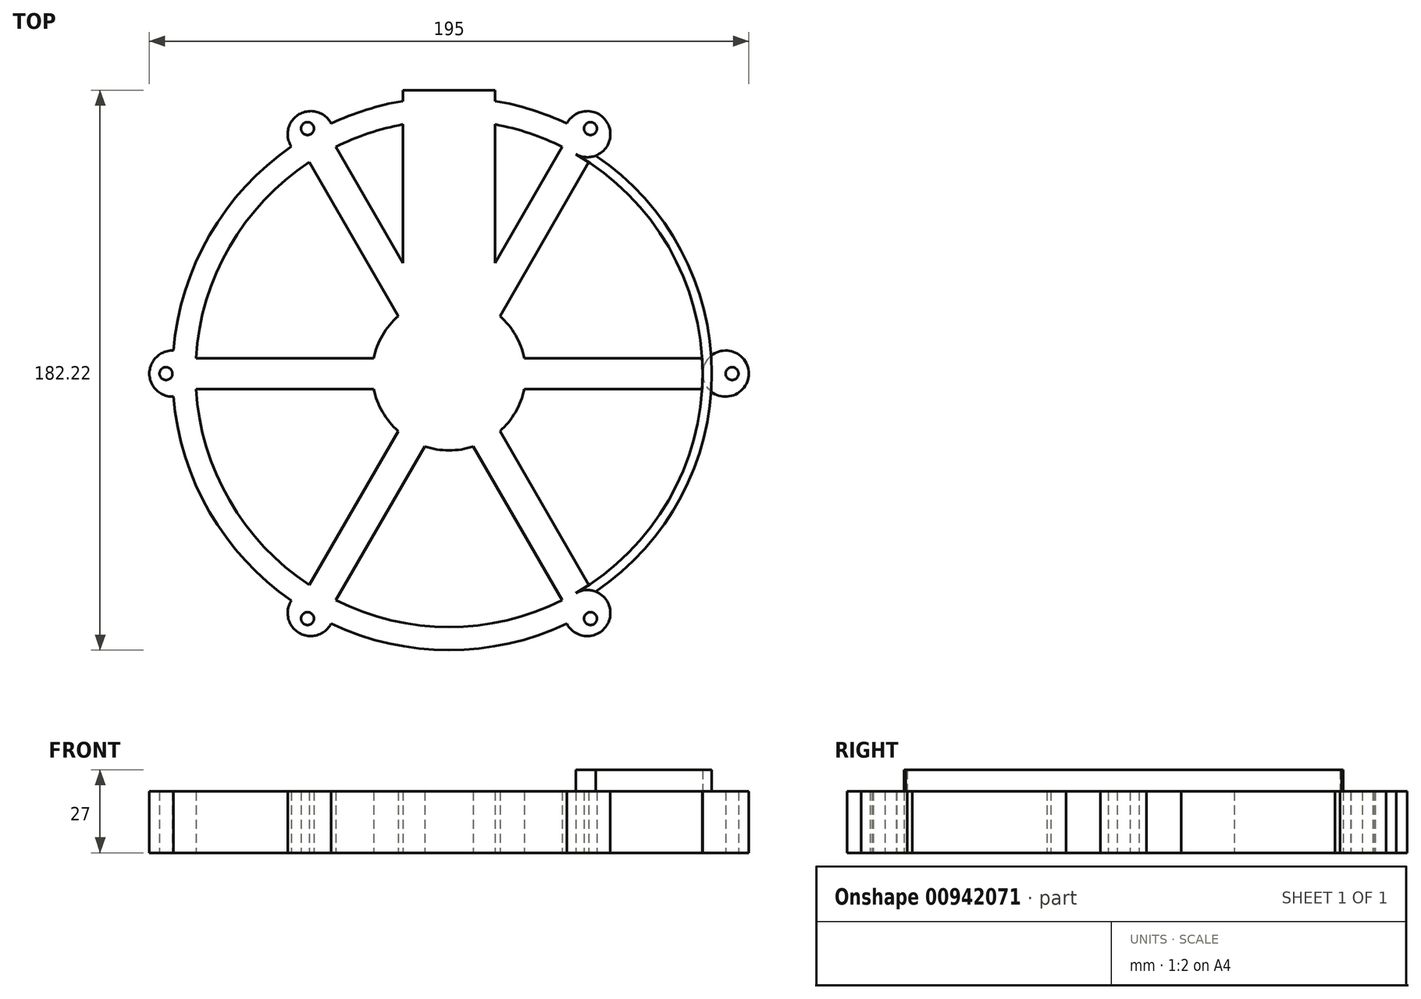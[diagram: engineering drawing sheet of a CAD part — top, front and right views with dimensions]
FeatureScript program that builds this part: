
annotation { "Feature Type Name" : "Feature", "Feature Type Description" : "" }
export const myFeature = defineFeature(function(context is Context, id is Id, definition is map)
    precondition{}
    {
        {
            var Q0;
            Q0=qCreatedBy(makeId("Top.planeOp"),FACE);
            var sketch = newSketch(context, id + "F0", { "sketchPlane" : qUnion([Q0])});
            skCircle(sketch, "E0", {"center": v(0, 0) * mm, "radius": 90 * mm});
            skCircle(sketch, "E1", {"center": v(0, 0) * mm, "radius": 82.5 * mm});
            skCircle(sketch, "E2", {"center": v(0, 0) * mm, "radius": 25 * mm});
            skLineSegment(sketch, "E3", {"start": v(45.5, 68.82) * mm, "end": v(16.58, 18.71) * mm});
            skLineSegment(sketch, "E4.MirrorCS", {"start": v(36.84, 73.82) * mm, "end": v(7.92, 23.71) * mm});
            skLineSegment(sketch, "E5.1.0", {"start": v(-36.84, 73.82) * mm, "end": v(-7.92, 23.71) * mm});
            skLineSegment(sketch, "E5.1.1", {"start": v(-45.5, 68.82) * mm, "end": v(-16.58, 18.71) * mm});
            skLineSegment(sketch, "E5.2.0", {"start": v(-82.35, 5) * mm, "end": v(-24.5, 5) * mm});
            skLineSegment(sketch, "E5.2.1", {"start": v(-82.35, -5) * mm, "end": v(-24.5, -5) * mm});
            skLineSegment(sketch, "E5.3.0", {"start": v(-45.5, -68.82) * mm, "end": v(-16.58, -18.71) * mm});
            skLineSegment(sketch, "E5.3.1", {"start": v(-36.84, -73.82) * mm, "end": v(-7.92, -23.71) * mm});
            skLineSegment(sketch, "E5.4.0", {"start": v(36.84, -73.82) * mm, "end": v(7.92, -23.71) * mm});
            skLineSegment(sketch, "E5.4.1", {"start": v(45.5, -68.82) * mm, "end": v(16.58, -18.71) * mm});
            skLineSegment(sketch, "E5.5.0", {"start": v(82.35, -5) * mm, "end": v(24.5, -5) * mm});
            skLineSegment(sketch, "E5.5.1", {"start": v(82.35, 5) * mm, "end": v(24.5, 5) * mm});
            skCircle(sketch, "E6", {"center": v(45, 77.94) * mm, "radius": 7.5 * mm});
            skCircle(sketch, "E7", {"center": v(46.05, 79.76) * mm, "radius": 2.1 * mm});
            skCircle(sketch, "E8.1.0", {"center": v(-45, 77.94) * mm, "radius": 7.5 * mm});
            skCircle(sketch, "E8.1.1", {"center": v(-46.05, 79.76) * mm, "radius": 2.1 * mm});
            skCircle(sketch, "E8.2.0", {"center": v(-90, 0) * mm, "radius": 7.5 * mm});
            skCircle(sketch, "E8.2.1", {"center": v(-92.1, 0) * mm, "radius": 2.1 * mm});
            skCircle(sketch, "E8.3.0", {"center": v(-45, -77.94) * mm, "radius": 7.5 * mm});
            skCircle(sketch, "E8.3.1", {"center": v(-46.05, -79.76) * mm, "radius": 2.1 * mm});
            skCircle(sketch, "E8.4.0", {"center": v(45, -77.94) * mm, "radius": 7.5 * mm});
            skCircle(sketch, "E8.4.1", {"center": v(46.05, -79.76) * mm, "radius": 2.1 * mm});
            skCircle(sketch, "E8.5.0", {"center": v(90, 0) * mm, "radius": 7.5 * mm});
            skCircle(sketch, "E8.5.1", {"center": v(92.1, 0) * mm, "radius": 2.1 * mm});
            skLineSegment(sketch, "E9", {"start": v(15, 35.98) * mm, "end": v(15, 92.22) * mm});
            skLineSegment(sketch, "E10.MirrorCS", {"start": v(-15, 35.98) * mm, "end": v(-15, 92.22) * mm});
            skLineSegment(sketch, "E11", {"start": v(-15, 92.22) * mm, "end": v(15, 92.22) * mm});
            skSolve(sketch);
        }
        {
            var Q0;
            {var subQ4=sQuery(id+"F0.wireOp",EDGE,"E0");var subQ7=sQuery(id+"F0.wireOp",EDGE,"E8.1.0");var subQ9=makeQuery(id+"F0.imprint","INTERSECT",VERTEX,{"disambiguationData":[OD(1.0)],"derivedFrom":[subQ4,subQ7]});Q0=makeQuery(id+"F0.imprint","IMPRINT",FACE,{"disambiguationData":[TD([[makeQuery(id+"F0.imprint","IMPRINT",EDGE,{"disambiguationData":[TD([[subQ9,-1.0]])],"derivedFrom":subQ4}),1.0]])]});}
            var Q1;
            {var subQ0=sQuery(id+"F0.wireOp",EDGE,"E8.1.0");var subQ1=sQuery(id+"F0.wireOp",EDGE,"E0");var subQ2=makeQuery(id+"F0.imprint","INTERSECT",VERTEX,{"disambiguationData":[OD(0.0)],"derivedFrom":[subQ1,subQ0]});Q1=makeQuery(id+"F0.imprint","IMPRINT",FACE,{"disambiguationData":[TD([[makeQuery(id+"F0.imprint","IMPRINT",EDGE,{"disambiguationData":[TD([[subQ2,-1.0]])],"derivedFrom":subQ1}),1.0]])]});}
            var Q2;
            {var subQ3=sQuery(id+"F0.wireOp",EDGE,"E8.1.1");Q2=makeQuery(id+"F0.imprint","IMPRINT",FACE,{"disambiguationData":[TD([[makeQuery(id+"F0.imprint","IMPRINT",EDGE,{"derivedFrom":subQ3}),-1.0]])]});}
            var Q3;
            {var subQ1=sQuery(id+"F0.wireOp",EDGE,"E0");var subQ6=sQuery(id+"F0.wireOp",EDGE,"E10.MirrorCS");var subQ8=makeQuery(id+"F0.imprint","INTERSECT",VERTEX,{"derivedFrom":[subQ1,subQ6]});Q3=makeQuery(id+"F0.imprint","IMPRINT",FACE,{"disambiguationData":[TD([[makeQuery(id+"F0.imprint","IMPRINT",EDGE,{"disambiguationData":[TD([[subQ8,-1.0]])],"derivedFrom":subQ1}),1.0]])]});}
            var Q4;
            {var subQ0=sQuery(id+"F0.wireOp",EDGE,"E9");var subQ1=sQuery(id+"F0.wireOp",EDGE,"E0");var subQ2=makeQuery(id+"F0.imprint","INTERSECT",VERTEX,{"derivedFrom":[subQ1,subQ0]});Q4=makeQuery(id+"F0.imprint","IMPRINT",FACE,{"disambiguationData":[TD([[makeQuery(id+"F0.imprint","IMPRINT",EDGE,{"disambiguationData":[TD([[subQ2,-1.0]])],"derivedFrom":subQ1}),1.0]])]});}
            var Q5;
            {var subQ5=sQuery(id+"F0.wireOp",EDGE,"E11");Q5=makeQuery(id+"F0.imprint","IMPRINT",FACE,{"disambiguationData":[TD([[makeQuery(id+"F0.imprint","IMPRINT",EDGE,{"derivedFrom":subQ5}),-1.0]])]});}
            var Q6;
            {var subQ0=sQuery(id+"F0.wireOp",EDGE,"E6");var subQ1=sQuery(id+"F0.wireOp",EDGE,"E0");var subQ2=makeQuery(id+"F0.imprint","INTERSECT",VERTEX,{"disambiguationData":[OD(1.0)],"derivedFrom":[subQ1,subQ0]});Q6=makeQuery(id+"F0.imprint","IMPRINT",FACE,{"disambiguationData":[TD([[makeQuery(id+"F0.imprint","IMPRINT",EDGE,{"disambiguationData":[TD([[subQ2,-1.0]])],"derivedFrom":subQ1}),1.0]])]});}
            var Q7;
            {var subQ0=sQuery(id+"F0.wireOp",EDGE,"E6");var subQ1=sQuery(id+"F0.wireOp",EDGE,"E0");var subQ2=makeQuery(id+"F0.imprint","INTERSECT",VERTEX,{"disambiguationData":[OD(0.0)],"derivedFrom":[subQ1,subQ0]});Q7=makeQuery(id+"F0.imprint","IMPRINT",FACE,{"disambiguationData":[TD([[makeQuery(id+"F0.imprint","IMPRINT",EDGE,{"disambiguationData":[TD([[subQ2,-1.0]])],"derivedFrom":subQ1}),1.0]])]});}
            var Q8;
            {var subQ3=sQuery(id+"F0.wireOp",EDGE,"E7");Q8=makeQuery(id+"F0.imprint","IMPRINT",FACE,{"disambiguationData":[TD([[makeQuery(id+"F0.imprint","IMPRINT",EDGE,{"derivedFrom":subQ3}),-1.0]])]});}
            var Q9;
            {var subQ4=sQuery(id+"F0.wireOp",EDGE,"E0");var subQ7=sQuery(id+"F0.wireOp",EDGE,"E8.5.0");var subQ9=makeQuery(id+"F0.imprint","INTERSECT",VERTEX,{"disambiguationData":[OD(1.0)],"derivedFrom":[subQ4,subQ7]});Q9=makeQuery(id+"F0.imprint","IMPRINT",FACE,{"disambiguationData":[TD([[makeQuery(id+"F0.imprint","IMPRINT",EDGE,{"disambiguationData":[TD([[subQ9,-1.0]])],"derivedFrom":subQ4}),1.0]])]});}
            var Q10;
            {var subQ0=sQuery(id+"F0.wireOp",EDGE,"E0");var subQ1=makeQuery(id+"F0.imprint","INTERSECT",VERTEX,{"derivedFrom":[subQ0,sQuery(id+"F0.wireOp",EDGE,"E8.5.1")]});Q10=makeQuery(id+"F0.imprint","IMPRINT",FACE,{"disambiguationData":[TD([[makeQuery(id+"F0.imprint","IMPRINT",EDGE,{"disambiguationData":[TD([[subQ1,1.0]])],"derivedFrom":subQ0}),1.0]])]});}
            var Q11;
            {var subQ0=sQuery(id+"F0.wireOp",EDGE,"E8.5.1");Q11=makeQuery(id+"F0.imprint","IMPRINT",FACE,{"disambiguationData":[TD([[makeQuery(id+"F0.imprint","IMPRINT",EDGE,{"derivedFrom":subQ0}),-1.0]])]});}
            var Q12;
            {var subQ4=sQuery(id+"F0.wireOp",EDGE,"E0");var subQ7=sQuery(id+"F0.wireOp",EDGE,"E8.5.0");var subQ9=makeQuery(id+"F0.imprint","INTERSECT",VERTEX,{"disambiguationData":[OD(0.0)],"derivedFrom":[subQ4,subQ7]});Q12=makeQuery(id+"F0.imprint","IMPRINT",FACE,{"disambiguationData":[TD([[makeQuery(id+"F0.imprint","IMPRINT",EDGE,{"disambiguationData":[TD([[subQ9,1.0]])],"derivedFrom":subQ4}),1.0]])]});}
            var Q13;
            {var subQ5=sQuery(id+"F0.wireOp",EDGE,"E8.3.0");var subQ7=sQuery(id+"F0.wireOp",EDGE,"E0");var subQ8=makeQuery(id+"F0.imprint","INTERSECT",VERTEX,{"disambiguationData":[OD(1.0)],"derivedFrom":[subQ7,subQ5]});Q13=makeQuery(id+"F0.imprint","IMPRINT",FACE,{"disambiguationData":[TD([[makeQuery(id+"F0.imprint","IMPRINT",EDGE,{"disambiguationData":[TD([[subQ8,-1.0]])],"derivedFrom":subQ7}),1.0]])]});}
            var Q14;
            {var subQ0=sQuery(id+"F0.wireOp",EDGE,"E8.4.0");var subQ1=sQuery(id+"F0.wireOp",EDGE,"E0");var subQ2=makeQuery(id+"F0.imprint","INTERSECT",VERTEX,{"disambiguationData":[OD(0.0)],"derivedFrom":[subQ1,subQ0]});Q14=makeQuery(id+"F0.imprint","IMPRINT",FACE,{"disambiguationData":[TD([[makeQuery(id+"F0.imprint","IMPRINT",EDGE,{"disambiguationData":[TD([[subQ2,-1.0]])],"derivedFrom":subQ1}),1.0]])]});}
            var Q15;
            {var subQ3=sQuery(id+"F0.wireOp",EDGE,"E8.4.1");Q15=makeQuery(id+"F0.imprint","IMPRINT",FACE,{"disambiguationData":[TD([[makeQuery(id+"F0.imprint","IMPRINT",EDGE,{"derivedFrom":subQ3}),-1.0]])]});}
            var Q16;
            {var subQ0=sQuery(id+"F0.wireOp",EDGE,"E8.3.0");var subQ1=sQuery(id+"F0.wireOp",EDGE,"E0");var subQ2=makeQuery(id+"F0.imprint","INTERSECT",VERTEX,{"disambiguationData":[OD(0.0)],"derivedFrom":[subQ1,subQ0]});Q16=makeQuery(id+"F0.imprint","IMPRINT",FACE,{"disambiguationData":[TD([[makeQuery(id+"F0.imprint","IMPRINT",EDGE,{"disambiguationData":[TD([[subQ2,-1.0]])],"derivedFrom":subQ1}),1.0]])]});}
            var Q17;
            {var subQ3=sQuery(id+"F0.wireOp",EDGE,"E8.3.1");Q17=makeQuery(id+"F0.imprint","IMPRINT",FACE,{"disambiguationData":[TD([[makeQuery(id+"F0.imprint","IMPRINT",EDGE,{"derivedFrom":subQ3}),-1.0]])]});}
            var Q18;
            {var subQ5=sQuery(id+"F0.wireOp",EDGE,"E8.2.0");var subQ7=sQuery(id+"F0.wireOp",EDGE,"E0");var subQ8=makeQuery(id+"F0.imprint","INTERSECT",VERTEX,{"disambiguationData":[OD(1.0)],"derivedFrom":[subQ7,subQ5]});Q18=makeQuery(id+"F0.imprint","IMPRINT",FACE,{"disambiguationData":[TD([[makeQuery(id+"F0.imprint","IMPRINT",EDGE,{"disambiguationData":[TD([[subQ8,-1.0]])],"derivedFrom":subQ7}),1.0]])]});}
            var Q19;
            {var subQ0=sQuery(id+"F0.wireOp",EDGE,"E8.2.0");var subQ1=sQuery(id+"F0.wireOp",EDGE,"E0");var subQ2=makeQuery(id+"F0.imprint","INTERSECT",VERTEX,{"disambiguationData":[OD(0.0)],"derivedFrom":[subQ1,subQ0]});Q19=makeQuery(id+"F0.imprint","IMPRINT",FACE,{"disambiguationData":[TD([[makeQuery(id+"F0.imprint","IMPRINT",EDGE,{"disambiguationData":[TD([[subQ2,-1.0]])],"derivedFrom":subQ1}),1.0]])]});}
            var Q20;
            {var subQ3=sQuery(id+"F0.wireOp",EDGE,"E8.2.1");Q20=makeQuery(id+"F0.imprint","IMPRINT",FACE,{"disambiguationData":[TD([[makeQuery(id+"F0.imprint","IMPRINT",EDGE,{"derivedFrom":subQ3}),-1.0]])]});}
            var Q21;
            {var subQ0=sQuery(id+"F0.wireOp",EDGE,"E5.2.0");Q21=makeQuery(id+"F0.imprint","IMPRINT",FACE,{"disambiguationData":[TD([[makeQuery(id+"F0.imprint","IMPRINT",EDGE,{"derivedFrom":subQ0}),-1.0]])]});}
            var Q22;
            {var subQ0=sQuery(id+"F0.wireOp",EDGE,"E5.3.0");Q22=makeQuery(id+"F0.imprint","IMPRINT",FACE,{"disambiguationData":[TD([[makeQuery(id+"F0.imprint","IMPRINT",EDGE,{"derivedFrom":subQ0}),-1.0]])]});}
            var Q23;
            {var subQ0=sQuery(id+"F0.wireOp",EDGE,"E5.4.0");Q23=makeQuery(id+"F0.imprint","IMPRINT",FACE,{"disambiguationData":[TD([[makeQuery(id+"F0.imprint","IMPRINT",EDGE,{"derivedFrom":subQ0}),-1.0]])]});}
            var Q24;
            {var subQ0=sQuery(id+"F0.wireOp",EDGE,"E5.5.0");Q24=makeQuery(id+"F0.imprint","IMPRINT",FACE,{"disambiguationData":[TD([[makeQuery(id+"F0.imprint","IMPRINT",EDGE,{"derivedFrom":subQ0}),-1.0]])]});}
            var Q25;
            {var subQ0=sQuery(id+"F0.wireOp",EDGE,"E3");Q25=makeQuery(id+"F0.imprint","IMPRINT",FACE,{"disambiguationData":[TD([[makeQuery(id+"F0.imprint","IMPRINT",EDGE,{"derivedFrom":subQ0}),-1.0]])]});}
            var Q26;
            {var subQ6=sQuery(id+"F0.wireOp",EDGE,"E5.1.1");Q26=makeQuery(id+"F0.imprint","IMPRINT",FACE,{"disambiguationData":[TD([[makeQuery(id+"F0.imprint","IMPRINT",EDGE,{"derivedFrom":subQ6}),1.0]])]});}
            var Q27;
            {var subQ0=sQuery(id+"F0.wireOp",EDGE,"E2");var subQ8=makeQuery(id+"F0.imprint","INTERSECT",VERTEX,{"derivedFrom":[subQ0,sQuery(id+"F0.wireOp",EDGE,"E5.5.0")]});Q27=makeQuery(id+"F0.imprint","IMPRINT",FACE,{"disambiguationData":[TD([[makeQuery(id+"F0.imprint","IMPRINT",EDGE,{"disambiguationData":[TD([[subQ8,-1.0]])],"derivedFrom":subQ0}),1.0]])]});}
            var Q28;
            {var subQ3=sQuery(id+"F0.wireOp",EDGE,"E9");var subQ9=sQuery(id+"F0.wireOp",EDGE,"E1");var subQ10=makeQuery(id+"F0.imprint","INTERSECT",VERTEX,{"derivedFrom":[subQ9,subQ3]});Q28=makeQuery(id+"F0.imprint","IMPRINT",FACE,{"disambiguationData":[TD([[makeQuery(id+"F0.imprint","IMPRINT",EDGE,{"disambiguationData":[TD([[subQ10,-1.0]])],"derivedFrom":subQ9}),1.0]])]});}
            extrude(context, id + "F1", {"entities" : qUnion([Q0, Q1, Q2, Q3, Q4, Q5, Q6, Q7, Q8, Q9, Q10, Q11, Q12, Q13, Q14, Q15, Q16, Q17, Q18, Q19, Q20, Q21, Q22, Q23, Q24, Q25, Q26, Q27, Q28]), "depth" : 20 * mm, "offsetDistance" : 25 * mm});
        }
        {
            var Q0;
            Q0=makeQuery(id+"F1.opExtrude","CAP_FACE",FACE,{"disambiguationData":[OSD([sQuery(id+"F0.wireOp",EDGE,"E0"),sQuery(id+"F0.wireOp",EDGE,"E1"),sQuery(id+"F0.wireOp",EDGE,"E2"),sQuery(id+"F0.wireOp",EDGE,"E3"),sQuery(id+"F0.wireOp",EDGE,"E4.MirrorCS"),sQuery(id+"F0.wireOp",EDGE,"E5.1.0"),sQuery(id+"F0.wireOp",EDGE,"E5.1.1"),sQuery(id+"F0.wireOp",EDGE,"E5.2.0"),sQuery(id+"F0.wireOp",EDGE,"E5.2.1"),sQuery(id+"F0.wireOp",EDGE,"E5.3.0"),sQuery(id+"F0.wireOp",EDGE,"E5.3.1"),sQuery(id+"F0.wireOp",EDGE,"E5.4.0"),sQuery(id+"F0.wireOp",EDGE,"E5.4.1"),sQuery(id+"F0.wireOp",EDGE,"E5.5.0"),sQuery(id+"F0.wireOp",EDGE,"E5.5.1"),sQuery(id+"F0.wireOp",EDGE,"E6"),sQuery(id+"F0.wireOp",EDGE,"E7"),sQuery(id+"F0.wireOp",EDGE,"E8.1.0"),sQuery(id+"F0.wireOp",EDGE,"E8.1.1"),sQuery(id+"F0.wireOp",EDGE,"E8.2.0"),sQuery(id+"F0.wireOp",EDGE,"E8.2.1"),sQuery(id+"F0.wireOp",EDGE,"E8.3.0"),sQuery(id+"F0.wireOp",EDGE,"E8.3.1"),sQuery(id+"F0.wireOp",EDGE,"E8.4.0"),sQuery(id+"F0.wireOp",EDGE,"E8.4.1"),sQuery(id+"F0.wireOp",EDGE,"E8.5.0"),sQuery(id+"F0.wireOp",EDGE,"E8.5.1"),sQuery(id+"F0.wireOp",EDGE,"E9"),sQuery(id+"F0.wireOp",EDGE,"E10.MirrorCS"),sQuery(id+"F0.wireOp",EDGE,"E11")])],"isStart":false});
            var sketch = newSketch(context, id + "F2", { "sketchPlane" : qUnion([Q0])});
            skCircle(sketch, "E12.0", {"center": v(0, 0) * mm, "radius": 82.5 * mm});
            skCircle(sketch, "E13", {"center": v(0, 0) * mm, "radius": 85.5 * mm});
            skSolve(sketch);
        }
        {
            var Q0;
            Q0=makeQuery(id+"F2.imprint","IMPRINT",FACE,{"disambiguationData":[TD([[makeQuery(id+"F2.imprint","IMPRINT",EDGE,{"derivedFrom":sQuery(id+"F2.wireOp",EDGE,"E13")}),1.0]])]});
            extrude(context, id + "F3", {"entities" : qUnion([Q0]), "operationType" : NewBodyOperationType.ADD, "depth" : 7 * mm, "offsetDistance" : 25 * mm});
        }
    });
